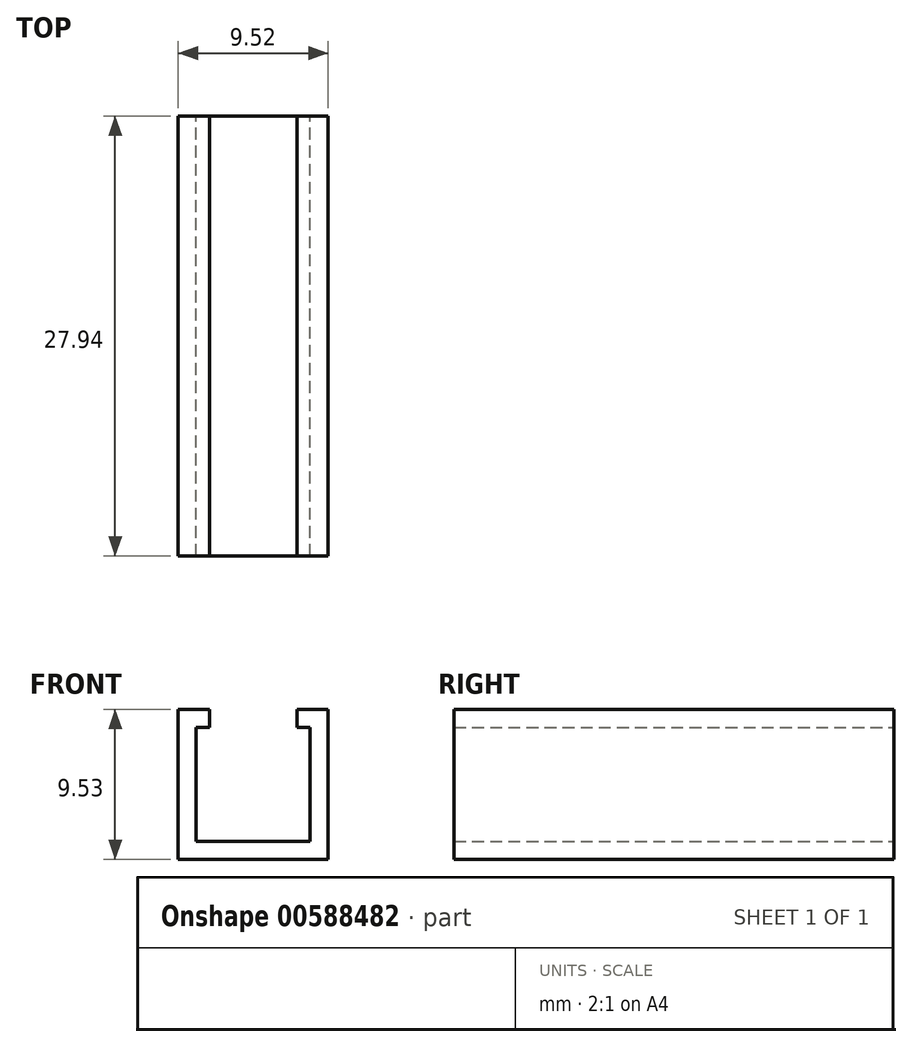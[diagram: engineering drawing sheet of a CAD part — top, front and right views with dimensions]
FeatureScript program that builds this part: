
annotation { "Feature Type Name" : "Feature", "Feature Type Description" : "" }
export const myFeature = defineFeature(function(context is Context, id is Id, definition is map)
    precondition{}
    {
        {
            var Q0;
            Q0=qCreatedBy(makeId("Front.planeOp"),FACE);
            var sketch = newSketch(context, id + "F0", { "sketchPlane" : qUnion([Q0])});
            skLineSegment(sketch, "E0", {"start": v(-4.76, 9.52) * mm, "end": v(-4.76, 0) * mm});
            skLineSegment(sketch, "E1", {"start": v(-4.76, 0) * mm, "end": v(4.76, 0) * mm});
            skLineSegment(sketch, "E2", {"start": v(4.76, 0) * mm, "end": v(4.76, 9.52) * mm});
            skLineSegment(sketch, "E3", {"start": v(4.76, 9.53) * mm, "end": v(3.62, 9.53) * mm});
            skLineSegment(sketch, "E4", {"start": v(3.62, 8.38) * mm, "end": v(3.62, 1.14) * mm});
            skLineSegment(sketch, "E5", {"start": v(3.62, 1.14) * mm, "end": v(-3.62, 1.14) * mm});
            skLineSegment(sketch, "E6", {"start": v(-3.62, 1.14) * mm, "end": v(-3.62, 8.38) * mm});
            skLineSegment(sketch, "E7", {"start": v(-3.62, 9.53) * mm, "end": v(-4.76, 9.53) * mm});
            skLineSegment(sketch, "E8", {"start": v(-3.62, 9.53) * mm, "end": v(-2.77, 9.53) * mm});
            skLineSegment(sketch, "E9", {"start": v(-2.77, 9.52) * mm, "end": v(-2.77, 8.38) * mm});
            skLineSegment(sketch, "E10", {"start": v(-2.77, 8.38) * mm, "end": v(-3.62, 8.38) * mm});
            skLineSegment(sketch, "E11", {"start": v(3.62, 9.53) * mm, "end": v(2.77, 9.53) * mm});
            skLineSegment(sketch, "E12", {"start": v(2.77, 9.52) * mm, "end": v(2.77, 8.38) * mm});
            skLineSegment(sketch, "E13", {"start": v(2.77, 8.38) * mm, "end": v(3.62, 8.38) * mm});
            skLineSegment(sketch, "E14", {"start": v(-3.62, 1.14) * mm, "end": v(-3.62, 0) * mm, "construction": true});
            skSolve(sketch);
        }
        {
            var Q0;
            Q0 = qSketchRegion(id + "F0", true);
            extrude(context, id + "F1", {"entities" : qUnion([Q0]), "depth" : 27.94 * mm, "offsetDistance" : 25.4 * mm});
        }
    });
